# Revit family: NBS_HeatraeSadia_StrgWtrHtrsElctrc_Express
name_source: partatom
category: Plumbing Fixtures
revit_build: Autodesk Revit 2014 (Build: 20130709_2115(x64)
units: mm (PartAtom-declared; Revit-internal decimal feet)

## types (3) — shared parameters
Accessories = Telescopic spout (95:970:103), 15 x 15 push fit connector for undersink fitting (95:970:110)
Arrangement = Single point – mains supply
AssetType = Fixed
CW Connection = Yes
CasingFinish = White stove enamel
Color = White
Connections = Supply direct from rising main or cistern, for oversink installations the inlet connection uses a 15 mm compression fitting
Controls = Valve
Depth = 250 mm  [stored 0.82021 ft]
Description = Vented point of use storage water heater
DurationUnit = year
Features = Fast heat up, complete with spout and valve, rod-type alloy sheathed element, quick and easy installation
Fixing = Wall fixed
FlowRate = To suit draw off requirements
HW Connection = No
IfcExportAs = IfcBoilerType
IfcExportType = WATER
IsWaterStorageHeater = Yes
ManufacturerName = Heatrae Sadia
ManufacturerURL = www.heatraesadia.com
Material = Outer casing: corrosion resistant steel; Heat unit: Rod-type alloy sheathed element mounted on a detachable plate
NBSCertification = http://www.nationalbimlibrary.com
NBSDescription = Storage water heaters, electric
NBSReference = 90-15-35/440
NominalLength = 263 mm  [stored 0.862861 ft]
NominalWidth = 250 mm  [stored 0.82021 ft]
OutletTemperatureRange = 5, 75
ProductInformation = www.heatraesadia.com/docs/344_084_POU-Vented_lit-AW_online.pdf
SafetyFeatures = Dry start cut-out
SpoutProjection = 358 mm
StorageWaterHeaterMaterial = NBS_Concept
ThermalInsulation = CFC/HCFC free (ODP zero) flame-retardant expanded polyurethane
ThirdPartyCertification = BEAB approved, Kiwa approved
Uniclass2 = 90-90-46/428
Uniclass2015Description = Electric storage water heaters
Uniclass2015Reference = Pr_60_60_96_28
Uniclass2015Version = Products v1.1
Vent Connection = No
Version = 1
WarrantyDurationParts = 2
WarrantyDurationUnit = year
WarrantyStartDate = 1900-12-31T23:59:59
Waste Connection = No
Width = 263 mm  [stored 0.862861 ft]
zero-valued in all types: HeatOutput, NominalEfficiency, NominalEnergyConsumption, NominalPartLoadRatio

## per-type parameters (varying)
| type | BIMObjectName | BodyHeight | Height | ModelNumber | ModelReference | Name | NominalHeight | Rating | Size | WaterStorageCapacity | Weight |
| 7-1kW | NBS_HeatraeSadia_StorageWaterHeatersElectric_Express_7-1kW | 334 mm  [stored 1.0958 ft] | 499 mm  [stored 1.63714 ft] | 95:010:160 | Express 7 1kW | StorageWaterHeatersElectric_Express_7-1kW_HeatraeSadia | 499 mm  [stored 1.63714 ft] | 1 kW | 499 x 263 x 250 mm | 7 | 12 |
| 7-3kW | NBS_HeatraeSadia_StorageWaterHeatersElectric_Express_7-3kW | 334 mm  [stored 1.0958 ft] | 499 mm  [stored 1.63714 ft] | 95:010:161 | Express 7 3kW | StorageWaterHeatersElectric_Express_7-3kW_HeatraeSadia | 499 mm  [stored 1.63714 ft] | 3 kW | 499 x 263 x 250 mm | 7 | 12 |
| 15-3kW | NBS_HeatraeSadia_StorageWaterHeatersElectric_Express_15-3kW | 570 mm | 735 mm | 95:010:162 | Express 15 3kW | StorageWaterHeatersElectric_Express_15-3kW_HeatraeSadia | 735 mm | 3 kW | 748 x 263 x 250 mm | 15 | 23 |

note: [stored X ft] marks values corroborated as IEEE doubles in the binary element streams (Revit-internal decimal feet)

## geometry (parser evidence)
native form markers: Sweep x3
no freeform markers — native parametric forms only
